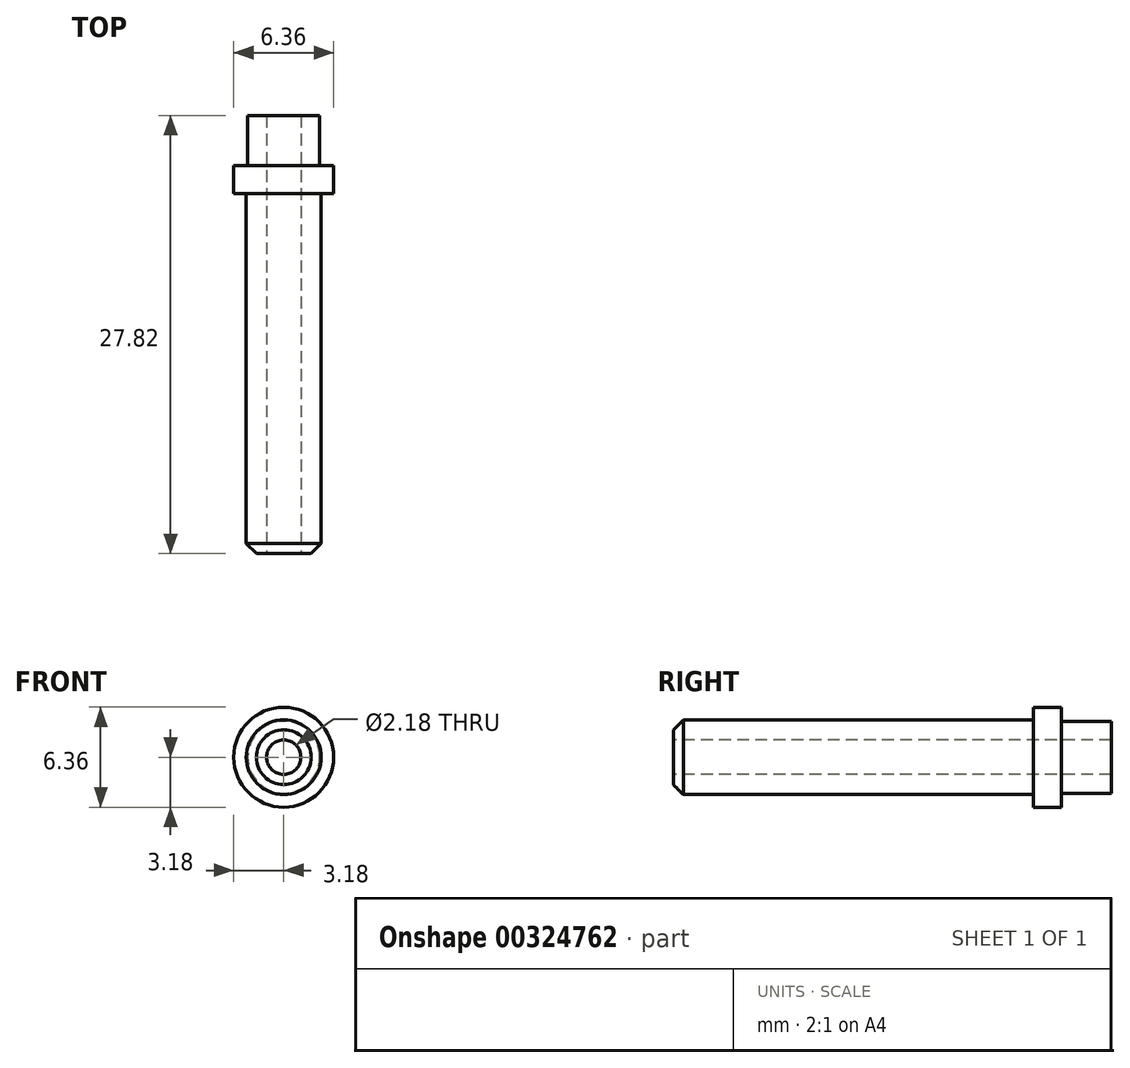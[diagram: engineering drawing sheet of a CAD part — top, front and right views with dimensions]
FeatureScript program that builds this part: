
annotation { "Feature Type Name" : "Feature", "Feature Type Description" : "" }
export const myFeature = defineFeature(function(context is Context, id is Id, definition is map)
    precondition{}
    {
        {
            var Q0;
            Q0=qCreatedBy(makeId("Front.planeOp"),FACE);
            var sketch = newSketch(context, id + "F0", { "sketchPlane" : qUnion([Q0])});
            skCircle(sketch, "E0", {"center": v(0, 0) * mm, "radius": 3.18 * mm});
            skSolve(sketch);
        }
        {
            var Q0;
            Q0=makeQuery(id+"F0.imprint","IMPRINT",FACE,{"disambiguationData":[TD([[makeQuery(id+"F0.imprint","IMPRINT",EDGE,{"derivedFrom":sQuery(id+"F0.wireOp",EDGE,"E0")}),1.0]])]});
            extrude(context, id + "F1", {"entities" : qUnion([Q0]), "depth" : 1.78 * mm, "offsetDistance" : 25.4 * mm});
        }
        {
            var Q0;
            Q0=makeQuery(id+"F1.opExtrude","CAP_FACE",FACE,{"disambiguationData":[OSD([sQuery(id+"F0.wireOp",EDGE,"E0")])],"isStart":false});
            var sketch = newSketch(context, id + "F2", { "sketchPlane" : qUnion([Q0])});
            skCircle(sketch, "E1", {"center": v(0, 0) * mm, "radius": 2.37 * mm});
            skSolve(sketch);
        }
        {
            var Q0;
            Q0=makeQuery(id+"F2.imprint","IMPRINT",FACE,{"disambiguationData":[TD([[makeQuery(id+"F2.imprint","IMPRINT",EDGE,{"derivedFrom":sQuery(id+"F2.wireOp",EDGE,"E1")}),1.0]])]});
            extrude(context, id + "F3", {"entities" : qUnion([Q0]), "operationType" : NewBodyOperationType.ADD, "depth" : 22.86 * mm, "offsetDistance" : 25.4 * mm});
        }
        {
            var Q0;
            Q0=makeQuery(id+"F1.opExtrude","CAP_FACE",FACE,{"disambiguationData":[OSD([sQuery(id+"F0.wireOp",EDGE,"E0")])],"isStart":true});
            var sketch = newSketch(context, id + "F4", { "sketchPlane" : qUnion([Q0])});
            skCircle(sketch, "E2", {"center": v(0, 0) * mm, "radius": 2.29 * mm});
            skSolve(sketch);
        }
        {
            var Q0;
            Q0=makeQuery(id+"F4.imprint","IMPRINT",FACE,{"disambiguationData":[TD([[makeQuery(id+"F4.imprint","IMPRINT",EDGE,{"derivedFrom":sQuery(id+"F4.wireOp",EDGE,"E2")}),1.0]])]});
            extrude(context, id + "F5", {"entities" : qUnion([Q0]), "operationType" : NewBodyOperationType.ADD, "depth" : 3.17 * mm, "offsetDistance" : 25.4 * mm});
        }
        {
            var Q0;
            Q0=makeQuery(id+"F3.opExtrude","CAP_FACE",FACE,{"disambiguationData":[OSD([sQuery(id+"F2.wireOp",EDGE,"E1")])],"isStart":false});
            var sketch = newSketch(context, id + "F6", { "sketchPlane" : qUnion([Q0])});
            skCircle(sketch, "E3", {"center": v(0, 0) * mm, "radius": 1.1 * mm});
            skSolve(sketch);
        }
        {
            var Q0;
            Q0=makeQuery(id+"F6.imprint","IMPRINT",FACE,{"disambiguationData":[TD([[makeQuery(id+"F6.imprint","IMPRINT",EDGE,{"derivedFrom":sQuery(id+"F6.wireOp",EDGE,"E3")}),1.0]])]});
            extrude(context, id + "F7", {"entities" : qUnion([Q0]), "operationType" : NewBodyOperationType.REMOVE, "endBound" : BoundingType.THROUGH_ALL, "oppositeDirection" : true, "depth" : 25.4 * mm, "offsetDistance" : 25.4 * mm});
        }
        {
            var Q0;
            Q0=makeQuery(id+"F3.opExtrude","CAP_EDGE",EDGE,{"disambiguationData":[OSD([sQuery(id+"F2.wireOp",EDGE,"E1")])],"isStart":false});
            chamfer(context, id + "F8", {"entities" : qUnion([Q0]), "width" : 0.64 * mm, "tangentPropagation" : true});
        }
    });
